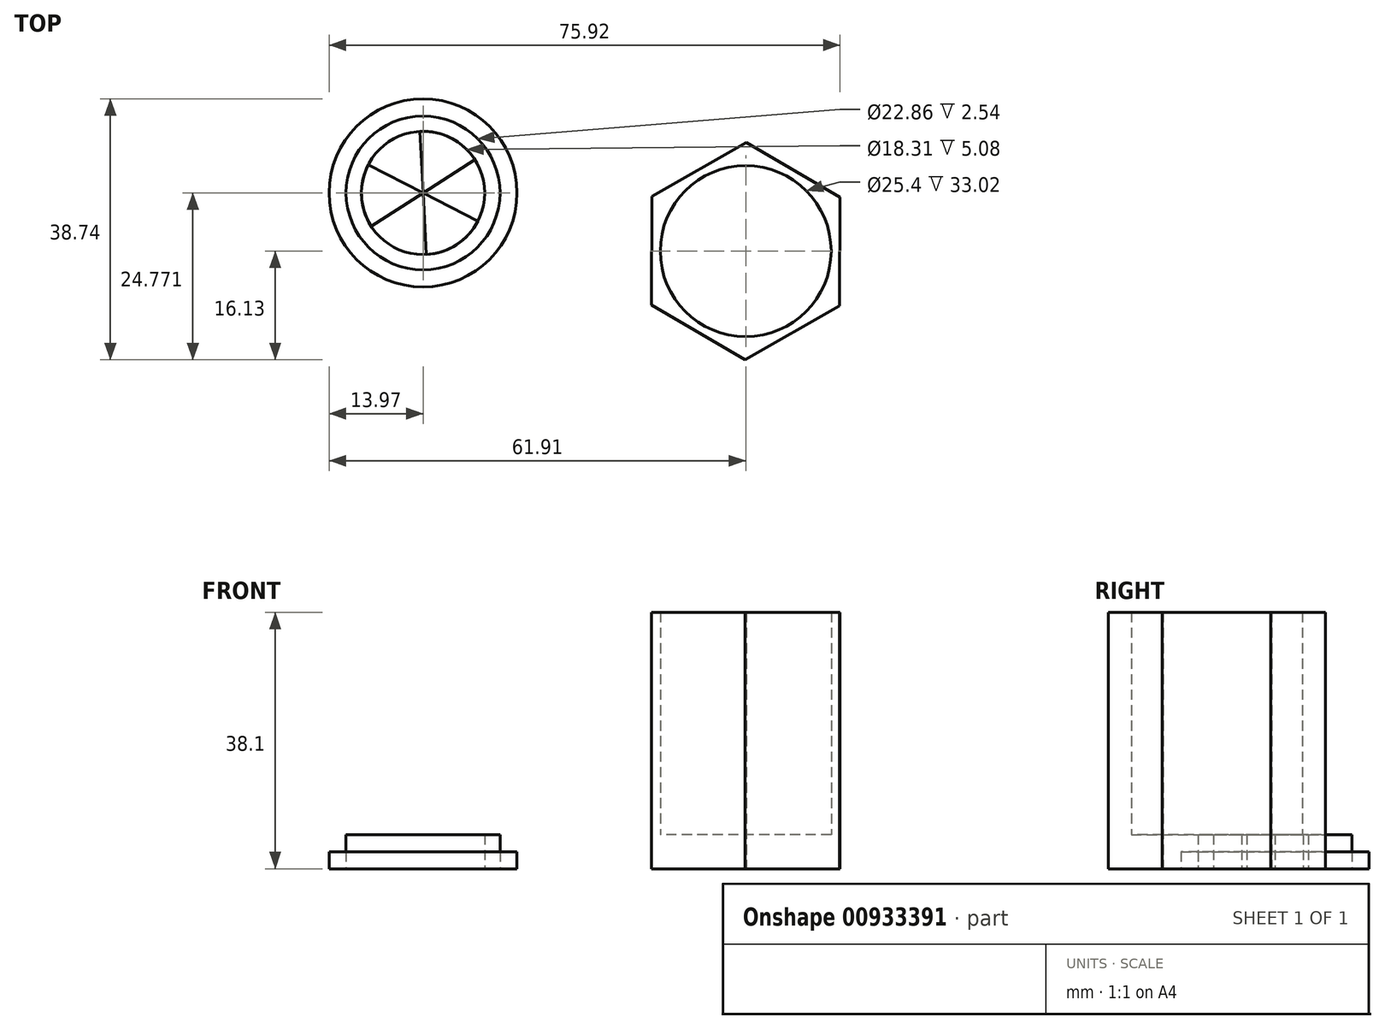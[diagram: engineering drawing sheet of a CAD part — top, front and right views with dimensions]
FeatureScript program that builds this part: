
annotation { "Feature Type Name" : "Feature", "Feature Type Description" : "" }
export const myFeature = defineFeature(function(context is Context, id is Id, definition is map)
    precondition{}
    {
        {
            var Q0;
            Q0=qCreatedBy(makeId("Top.planeOp"),FACE);
            var sketch = newSketch(context, id + "F0", { "sketchPlane" : qUnion([Q0])});
            skCircle(sketch, "E0.cCircle", {"center": v(0, 0) * mm, "radius": 13.97 * mm, "construction": true});
            skLineSegment(sketch, "E0.0", {"start": v(0.07, 16.13) * mm, "end": v(14, 8) * mm});
            skLineSegment(sketch, "E0.1", {"start": v(14, 8) * mm, "end": v(13.93, -8.13) * mm});
            skLineSegment(sketch, "E0.2", {"start": v(13.93, -8.13) * mm, "end": v(-0.07, -16.13) * mm});
            skLineSegment(sketch, "E0.3", {"start": v(-0.07, -16.13) * mm, "end": v(-14, -8) * mm});
            skLineSegment(sketch, "E0.4", {"start": v(-14, -8) * mm, "end": v(-13.93, 8.13) * mm});
            skLineSegment(sketch, "E0.5", {"start": v(-13.93, 8.13) * mm, "end": v(0.07, 16.13) * mm});
            skPoint(sketch, "E0.0.midPoint", {"position": v(7.04, 12.07) * mm});
            skCircle(sketch, "E1", {"center": v(0, 0) * mm, "radius": 12.7 * mm});
            skLineSegment(sketch, "E2", {"start": v(-6.93, 12.13) * mm, "end": v(6.93, -12.13) * mm});
            skSolve(sketch);
        }
        {
            var Q0;
            Q0 = qSketchRegion(id + "F0", true);
            extrude(context, id + "F1", {"entities" : qUnion([Q0]), "depth" : 38.1 * mm, "offsetDistance" : 25.4 * mm});
        }
        {
            var Q0;
            Q0=makeQuery(id+"F0.imprint","IMPRINT",FACE,{"disambiguationData":[TD([[makeQuery(id+"F0.imprint","IMPRINT",EDGE,{"derivedFrom":sQuery(id+"F0.wireOp",EDGE,"E1")}),1.0]])]});
            extrude(context, id + "F2", {"entities" : qUnion([Q0]), "operationType" : NewBodyOperationType.ADD, "depth" : 5.08 * mm, "offsetDistance" : 25.4 * mm});
        }
        {
            var Q0;
            Q0=qCreatedBy(makeId("Top.planeOp"),FACE);
            var sketch = newSketch(context, id + "F3", { "sketchPlane" : qUnion([Q0])});
            skCircle(sketch, "E3", {"center": v(-47.94, 8.64) * mm, "radius": 11.43 * mm});
            skCircle(sketch, "E4", {"center": v(-47.94, 8.64) * mm, "radius": 13.97 * mm});
            skCircle(sketch, "E5", {"center": v(-47.94, 8.64) * mm, "radius": 9.16 * mm});
            skPoint(sketch, "E6.0.midPoint", {"position": v(-43.68, 2.04) * mm});
            skLineSegment(sketch, "E7", {"start": v(-48.4, 17.78) * mm, "end": v(-47.94, 8.64) * mm});
            skLineSegment(sketch, "E8", {"start": v(-56.08, 12.83) * mm, "end": v(-47.94, 8.64) * mm});
            skLineSegment(sketch, "E9", {"start": v(-55.63, 3.67) * mm, "end": v(-47.94, 8.64) * mm});
            skLineSegment(sketch, "E10", {"start": v(-47.47, -0.5) * mm, "end": v(-47.94, 8.64) * mm});
            skLineSegment(sketch, "E11", {"start": v(-39.8, 4.45) * mm, "end": v(-47.94, 8.64) * mm});
            skLineSegment(sketch, "E12", {"start": v(-40.25, 13.61) * mm, "end": v(-47.94, 8.64) * mm});
            skSolve(sketch);
        }
        {
            var Q0;
            Q0=makeQuery(id+"F3.imprint","IMPRINT",FACE,{"disambiguationData":[TD([[makeQuery(id+"F3.imprint","IMPRINT",EDGE,{"derivedFrom":sQuery(id+"F3.wireOp",EDGE,"E3")}),-1.0]])]});
            extrude(context, id + "F4", {"entities" : qUnion([Q0]), "depth" : 2.54 * mm, "offsetDistance" : 25.4 * mm});
        }
        {
            var Q0;
            {var subQ0=sQuery(id+"F3.wireOp",EDGE,"E7");Q0=makeQuery(id+"F3.imprint","IMPRINT",FACE,{"disambiguationData":[TD([[makeQuery(id+"F3.imprint","IMPRINT",EDGE,{"derivedFrom":subQ0}),1.0]])]});}
            var Q1;
            {var subQ0=sQuery(id+"F3.wireOp",EDGE,"E8");Q1=makeQuery(id+"F3.imprint","IMPRINT",FACE,{"disambiguationData":[TD([[makeQuery(id+"F3.imprint","IMPRINT",EDGE,{"derivedFrom":subQ0}),-1.0]])]});}
            var Q2;
            {var subQ0=sQuery(id+"F3.wireOp",EDGE,"E10");Q2=makeQuery(id+"F3.imprint","IMPRINT",FACE,{"disambiguationData":[TD([[makeQuery(id+"F3.imprint","IMPRINT",EDGE,{"derivedFrom":subQ0}),-1.0]])]});}
            extrude(context, id + "F5", {"entities" : qUnion([Q0, Q1, Q2]), "depth" : 5.08 * mm, "offsetDistance" : 25.4 * mm});
        }
        {
            var Q0;
            Q0=makeQuery(id+"F3.imprint","IMPRINT",FACE,{"disambiguationData":[TD([[makeQuery(id+"F3.imprint","IMPRINT",EDGE,{"derivedFrom":sQuery(id+"F3.wireOp",EDGE,"E3")}),1.0]])]});
            extrude(context, id + "F6", {"entities" : qUnion([Q0]), "depth" : 5.08 * mm, "offsetDistance" : 25.4 * mm});
        }
    });
